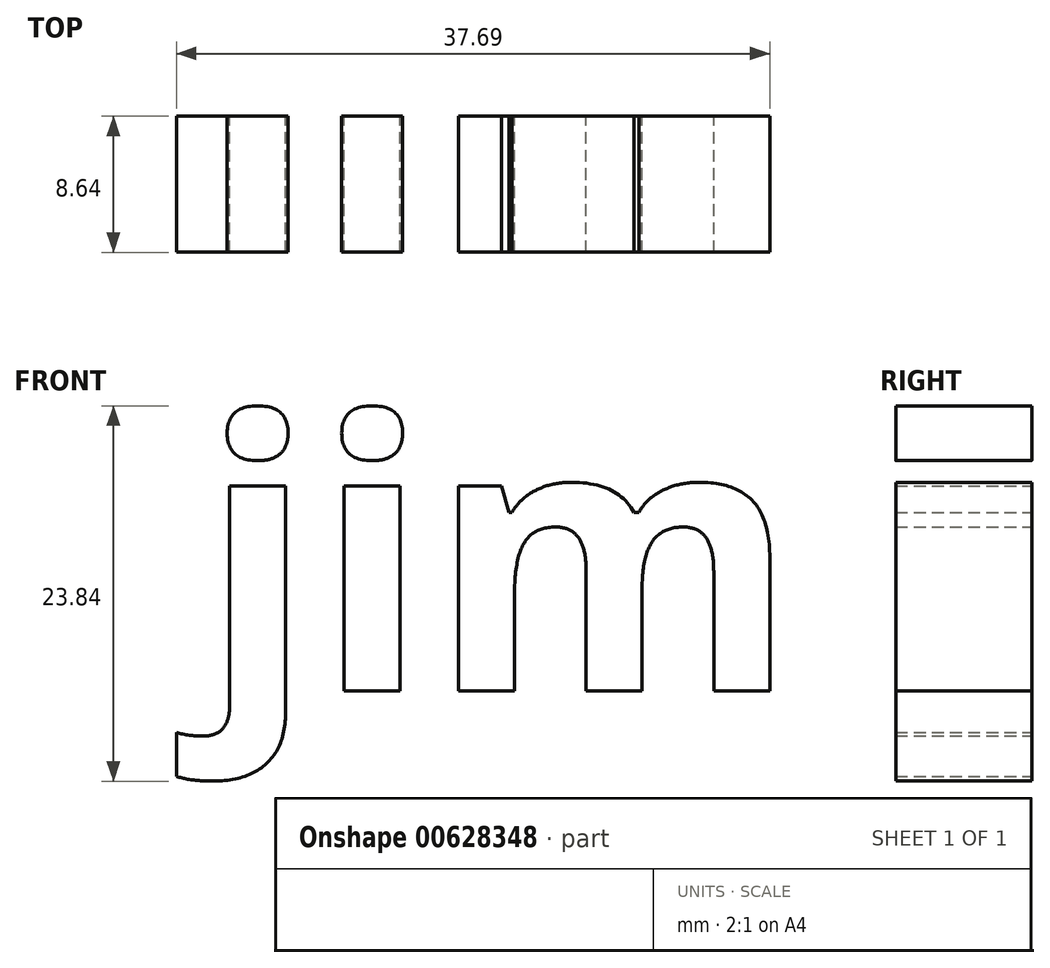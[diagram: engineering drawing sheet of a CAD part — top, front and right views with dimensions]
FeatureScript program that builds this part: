
annotation { "Feature Type Name" : "Feature", "Feature Type Description" : "" }
export const myFeature = defineFeature(function(context is Context, id is Id, definition is map)
    precondition{}
    {
        {
            var Q0;
            Q0=qCreatedBy(makeId("Front.planeOp"),FACE);
            var sketch = newSketch(context, id + "F0", { "sketchPlane" : qUnion([Q0])});
            skArc(sketch, "E0", {"start": v(-85.95, 29.36) * mm, "mid": v(-74.42, 11.68) * mm, "end": v(-72.1, 32.66) * mm});
            skText(sketch, "E1", { "text": "jim", "fontName": "OpenSans-Bold.ttf"});
            const initialGuessF0  = {"E1": [-0.016, 0.01749, 1, 0, 0.01716]};
            skSetInitialGuess(sketch, initialGuessF0);
            skSolve(sketch);
        }
        {
            var Q0;
            Q0 = qSketchRegion(id + "F0", true);
            extrude(context, id + "F1", {"entities" : qUnion([Q0]), "depth" : 8.64 * mm, "offsetDistance" : 25.4 * mm});
        }
    });
